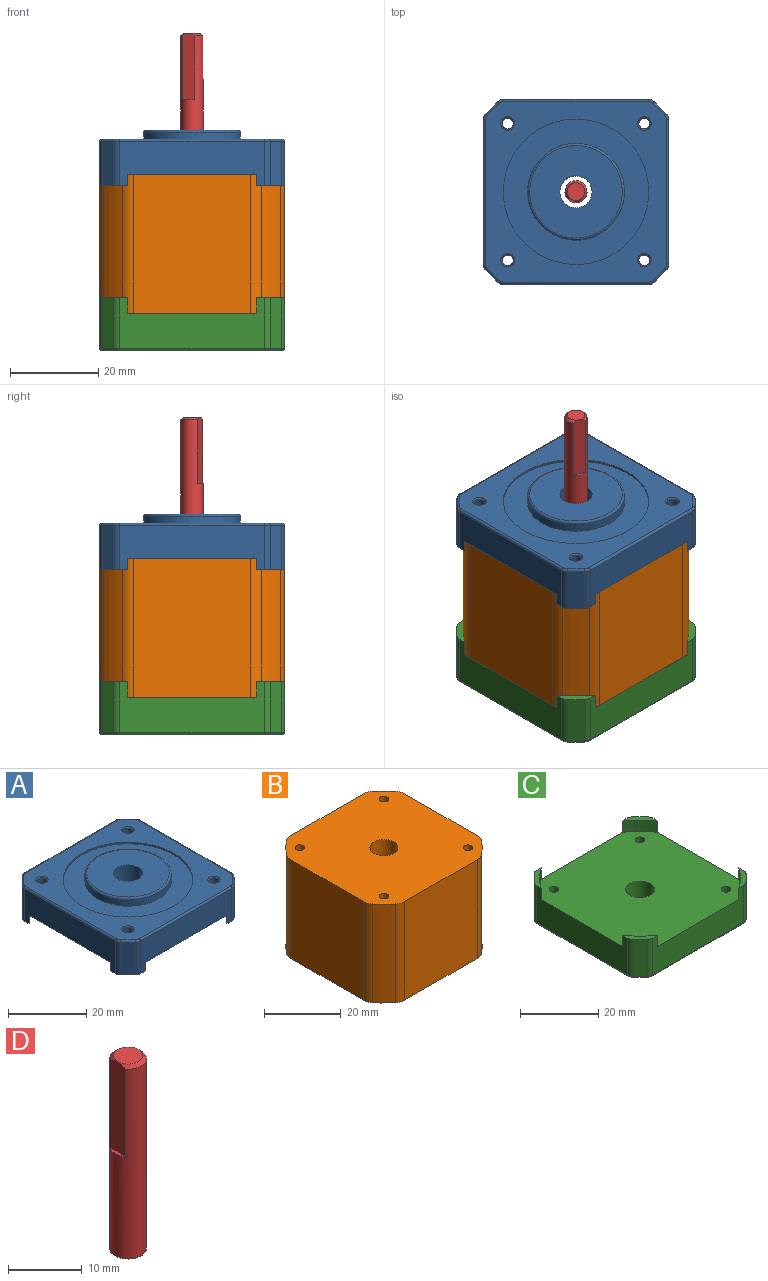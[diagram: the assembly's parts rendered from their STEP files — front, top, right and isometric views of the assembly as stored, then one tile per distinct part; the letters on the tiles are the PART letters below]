
ASSEMBLY  parts=4 mates=8
PART A: 56 faces, bbox 42.3x42.3x12.6 mm
  f0: plane 42x42mm, normal (0,0,-1), area 1631.2mm2, adj f2,f4,f6,f8,f9,f10,f11,f12
  f1: plane 10.1x2.63mm, normal (0.71,0.71,0), area 37.5mm2, adj f22,f27,f34,f39
  f2: plane 32.74x10.1mm, normal (0,1,0), area 254.6mm2, adj f0,f19,f20,f21,f22,f27,f28,f43
  f3: plane 10.1x2.63mm, normal (-0.71,0.71,0), area 37.5mm2, adj f20,f28,f29,f47
  f4: plane 32.74x10.1mm, normal (-1,0,0), area 254.6mm2, adj f0,f19,f20,f25,f26,f29,f30,f50
  f5: plane 10.1x2.63mm, normal (-0.71,-0.71,0), area 37.5mm2, adj f26,f30,f31,f46
  f6: plane 32.74x10.1mm, normal (0,-1,0), area 254.6mm2, adj f0,f23,f24,f25,f26,f31,f32,f42
  f7: plane 10.1x2.63mm, normal (0.71,-0.71,0), area 37.5mm2, adj f24,f32,f33,f38
  f8: cylinder r=1.25mm len=7.7mm, axis (0,0,-1), area 60.5mm2, adj f0,f54
  f9: cylinder r=1.25mm len=7.7mm, axis (0,0,-1), area 60.5mm2, adj f0,f55
  f10: cylinder r=1.25mm len=7.7mm, axis (0,0,-1), area 60.5mm2, adj f0,f52
  f11: cylinder r=3.65mm len=10mm, axis (0,0,-1), area 229.3mm2, adj f0,f16
  f12: cylinder r=1.25mm len=7.7mm, axis (0,0,-1), area 60.5mm2, adj f0,f53
  f13: plane 32.74x10.1mm, normal (1,0,0), area 254.6mm2, adj f0,f21,f22,f23,f24,f33,f34,f35
  f14: plane 41x41mm, normal (0,0,1), area 770.5mm2, adj f17,f35,f36,f37,f38,f39,f40,f41
  f15: cylinder r=11mm len=22mm, axis (0,0,-1), area 138.2mm2, adj f18,f51
  f16: plane 21x21mm, normal (0,0,1), area 304.5mm2, adj f11,f51
  f17: cylinder r=16.5mm len=33mm, axis (0,0,1), area 51.8mm2, adj f14,f18
  f18: plane 33x33mm, normal (0,0,1), area 475.2mm2, adj f15,f17
  f19: cylinder r=25.6mm len=6.36mm, axis (0,0,1), area 23.5mm2, adj f0,f2,f4,f20
  f20: plane 6.36x6.36mm, normal (0,0,-1), area 10.4mm2, adj f2,f3,f4,f19,f28,f29
  f21: cylinder r=25.6mm len=6.36mm, axis (0,0,1), area 23.5mm2, adj f0,f2,f13,f22
  f22: plane 6.36x6.36mm, normal (0,0,-1), area 10.4mm2, adj f1,f2,f13,f21,f27,f34
  f23: cylinder r=25.6mm len=6.36mm, axis (0,0,1), area 23.5mm2, adj f0,f6,f13,f24
  f24: plane 6.36x6.36mm, normal (0,0,-1), area 10.4mm2, adj f6,f7,f13,f23,f32,f33
  f25: cylinder r=25.6mm len=6.36mm, axis (0,0,1), area 23.5mm2, adj f0,f4,f6,f26
  f26: plane 6.36x6.36mm, normal (0,0,-1), area 10.4mm2, adj f4,f5,f6,f25,f30,f31
  f27: cylinder r=2mm len=10.1mm, axis (0,0,-1), area 15.9mm2, adj f1,f2,f22,f41
  f28: cylinder r=2mm len=10.1mm, axis (0,0,1), area 15.9mm2, adj f2,f3,f20,f45
  f29: cylinder r=2mm len=10.1mm, axis (0,0,-1), area 15.9mm2, adj f3,f4,f20,f49
  f30: cylinder r=2mm len=10.1mm, axis (0,0,1), area 15.9mm2, adj f4,f5,f26,f48
  f31: cylinder r=2mm len=10.1mm, axis (0,0,1), area 15.9mm2, adj f5,f6,f26,f44
  f32: cylinder r=2mm len=10.1mm, axis (0,0,-1), area 15.9mm2, adj f6,f7,f24,f40
  f33: cylinder r=2mm len=10.1mm, axis (0,0,1), area 15.9mm2, adj f7,f13,f24,f36
  f34: cylinder r=2mm len=10.1mm, axis (0,0,-1), area 15.9mm2, adj f1,f13,f22,f37
  f35: cylinder r=0.5mm len=32.74mm, axis (0,-1,0), area 25.7mm2, adj f13,f14,f36,f37
  f36: torus R=1.5mm, axis (0,0,1), area 1.1mm2, adj f14,f33,f35,f38
  f37: torus R=1.5mm, axis (0,0,1), area 1.1mm2, adj f14,f34,f35,f39
  f38: cylinder r=0.5mm len=2.98mm, axis (-0.71,-0.71,0), area 2.9mm2, adj f7,f14,f36,f40
  f39: cylinder r=0.5mm len=2.98mm, axis (0.71,-0.71,0), area 2.9mm2, adj f1,f14,f37,f41
  f40: torus R=1.5mm, axis (0,0,1), area 1.1mm2, adj f14,f32,f38,f42
  f41: torus R=1.5mm, axis (0,0,1), area 1.1mm2, adj f14,f27,f39,f43
  f42: cylinder r=0.5mm len=32.74mm, axis (-1,0,0), area 25.7mm2, adj f6,f14,f40,f44
  f43: cylinder r=0.5mm len=32.74mm, axis (1,0,0), area 25.7mm2, adj f2,f14,f41,f45
  f44: torus R=1.5mm, axis (0,0,1), area 1.1mm2, adj f14,f31,f42,f46
  f45: torus R=1.5mm, axis (0,0,1), area 1.1mm2, adj f14,f28,f43,f47
  f46: cylinder r=0.5mm len=2.98mm, axis (-0.71,0.71,0), area 2.9mm2, adj f5,f14,f44,f48
  f47: cylinder r=0.5mm len=2.98mm, axis (0.71,0.71,0), area 2.9mm2, adj f3,f14,f45,f49
  f48: torus R=1.5mm, axis (0,0,1), area 1.1mm2, adj f14,f30,f46,f50
  f49: torus R=1.5mm, axis (0,0,1), area 1.1mm2, adj f14,f29,f47,f50
  f50: cylinder r=0.5mm len=32.74mm, axis (0,1,0), area 25.7mm2, adj f4,f14,f48,f49
  f51: torus R=10.5mm, axis (0,0,1), area 53.4mm2, adj f15,f16
  f52: cone r=1.25mm half-angle=45deg, axis (0,0,1), area 3.7mm2, adj f10,f14
  f53: cone r=1.55mm half-angle=45deg, axis (0,0,1), area 3.7mm2, adj f12,f14
  f54: cone r=1.25mm half-angle=45deg, axis (0,0,1), area 3.7mm2, adj f8,f14
  f55: cone r=1.55mm half-angle=45deg, axis (0,0,1), area 3.7mm2, adj f9,f14
PART B: 23 faces, bbox 42x42x31.5 mm
  f0: cylinder r=25.6mm len=31.5mm, axis (0,0,1), area 194.5mm2, adj f13,f14,f15,f22
  f1: plane 31.5x26.65mm, normal (0,-1,0), area 839.5mm2, adj f13,f14,f15,f16
  f2: cylinder r=25.6mm len=31.5mm, axis (0,0,1), area 194.5mm2, adj f13,f14,f16,f17
  f3: plane 31.5x26.65mm, normal (-1,0,0), area 839.5mm2, adj f13,f14,f17,f18
  f4: cylinder r=25.6mm len=31.5mm, axis (0,0,1), area 194.5mm2, adj f13,f14,f18,f19
  f5: plane 31.5x26.65mm, normal (0,1,0), area 839.5mm2, adj f13,f14,f19,f20
  f6: cylinder r=25.6mm len=31.5mm, axis (0,0,1), area 194.5mm2, adj f13,f14,f20,f21
  f7: cylinder r=1.25mm len=31.5mm, axis (0,0,1), area 247.4mm2, adj f13,f14
  f8: plane 31.5x26.65mm, normal (1,0,0), area 839.5mm2, adj f13,f14,f21,f22
  f9: cylinder r=1.25mm len=31.5mm, axis (0,0,1), area 247.4mm2, adj f13,f14
  f10: cylinder r=1.25mm len=31.5mm, axis (0,0,1), area 247.4mm2, adj f13,f14
  f11: cylinder r=1.25mm len=31.5mm, axis (0,0,1), area 247.4mm2, adj f13,f14
  f12: cylinder r=3.65mm len=31.5mm, axis (0,0,1), area 722.4mm2, adj f13,f14
  f13: plane 42x42mm, normal (0,0,-1), area 1629.7mm2, adj f0,f1,f2,f3,f4,f5,f6,f7
  f14: plane 42x42mm, normal (0,0,1), area 1629.7mm2, adj f0,f1,f2,f3,f4,f5,f6,f7
  f15: cylinder r=4mm len=31.5mm, axis (0,0,1), area 83.8mm2, adj f0,f1,f13,f14
  f16: cylinder r=4mm len=31.5mm, axis (0,0,1), area 83.8mm2, adj f1,f2,f13,f14
  f17: cylinder r=4mm len=31.5mm, axis (0,0,1), area 83.8mm2, adj f2,f3,f13,f14
  f18: cylinder r=4mm len=31.5mm, axis (0,0,1), area 83.8mm2, adj f3,f4,f13,f14
  f19: cylinder r=4mm len=31.5mm, axis (0,0,1), area 83.8mm2, adj f4,f5,f13,f14
  f20: cylinder r=4mm len=31.5mm, axis (0,0,1), area 83.8mm2, adj f5,f6,f13,f14
  f21: cylinder r=4mm len=31.5mm, axis (0,0,1), area 83.8mm2, adj f6,f8,f13,f14
  f22: cylinder r=4mm len=31.5mm, axis (0,0,1), area 83.8mm2, adj f0,f8,f13,f14
PART C: 51 faces, bbox 42.3x42.3x12 mm
  f0: plane 42x42mm, normal (0,0,1), area 1631.2mm2, adj f1,f3,f5,f7,f8,f9,f10,f11
  f1: plane 32.74x11.5mm, normal (0,-1,0), area 274.1mm2, adj f0,f15,f16,f17,f18,f23,f26,f31
  f2: plane 11.5x2.63mm, normal (-0.71,-0.71,0), area 42.7mm2, adj f16,f23,f24,f35
  f3: plane 32.74x11.5mm, normal (-1,0,0), area 274.1mm2, adj f0,f15,f16,f21,f22,f24,f29,f39
  f4: plane 11.5x2.63mm, normal (-0.71,0.71,0), area 42.7mm2, adj f22,f29,f30,f43
  f5: plane 32.74x11.5mm, normal (0,1,0), area 274.1mm2, adj f0,f19,f20,f21,f22,f27,f30,f46
  f6: plane 11.5x2.63mm, normal (0.71,0.71,0), area 42.7mm2, adj f20,f27,f28,f42
  f7: plane 32.74x11.5mm, normal (1,0,0), area 274.1mm2, adj f0,f17,f18,f19,f20,f25,f28,f38
  f8: cylinder r=1.25mm len=6mm, axis (0,0,1), area 47.1mm2, adj f0,f48
  f9: cylinder r=3.65mm len=8.5mm, axis (0,0,1), area 194.9mm2, adj f0,f14
  f10: cylinder r=1.25mm len=6mm, axis (0,0,1), area 47.1mm2, adj f0,f47
  f11: cylinder r=1.25mm len=6mm, axis (0,0,1), area 47.1mm2, adj f0,f49
  f12: plane 11.5x2.63mm, normal (0.71,-0.71,0), area 42.7mm2, adj f18,f25,f26,f34
  f13: cylinder r=1.25mm len=6mm, axis (0,0,1), area 47.1mm2, adj f0,f50
  f14: plane 41x41mm, normal (0,0,-1), area 1437.4mm2, adj f9,f31,f32,f33,f34,f35,f36,f37
  f15: cylinder r=25.6mm len=6.36mm, axis (0,0,-1), area 31.6mm2, adj f0,f1,f3,f16
  f16: plane 6.36x6.36mm, normal (0,0,1), area 10.4mm2, adj f1,f2,f3,f15,f23,f24
  f17: cylinder r=25.6mm len=6.36mm, axis (0,0,-1), area 31.6mm2, adj f0,f1,f7,f18
  f18: plane 6.36x6.36mm, normal (0,0,1), area 10.4mm2, adj f1,f7,f12,f17,f25,f26
  f19: cylinder r=25.6mm len=6.36mm, axis (0,0,-1), area 31.6mm2, adj f0,f5,f7,f20
  f20: plane 6.36x6.36mm, normal (0,0,1), area 10.4mm2, adj f5,f6,f7,f19,f27,f28
  f21: cylinder r=25.6mm len=6.36mm, axis (0,0,-1), area 31.6mm2, adj f0,f3,f5,f22
  f22: plane 6.36x6.36mm, normal (0,0,1), area 10.4mm2, adj f3,f4,f5,f21,f29,f30
  f23: cylinder r=2mm len=11.5mm, axis (0,0,1), area 18.1mm2, adj f1,f2,f16,f33
  f24: cylinder r=2mm len=11.5mm, axis (0,0,1), area 18.1mm2, adj f2,f3,f16,f37
  f25: cylinder r=2mm len=11.5mm, axis (0,0,-1), area 18.1mm2, adj f7,f12,f18,f36
  f26: cylinder r=2mm len=11.5mm, axis (0,0,-1), area 18.1mm2, adj f1,f12,f18,f32
  f27: cylinder r=2mm len=11.5mm, axis (0,0,1), area 18.1mm2, adj f5,f6,f20,f44
  f28: cylinder r=2mm len=11.5mm, axis (0,0,1), area 18.1mm2, adj f6,f7,f20,f40
  f29: cylinder r=2mm len=11.5mm, axis (0,0,-1), area 18.1mm2, adj f3,f4,f22,f41
  f30: cylinder r=2mm len=11.5mm, axis (0,0,-1), area 18.1mm2, adj f4,f5,f22,f45
  f31: cylinder r=0.5mm len=32.74mm, axis (1,0,0), area 25.7mm2, adj f1,f14,f32,f33
  f32: torus R=1.5mm, axis (0,0,-1), area 1.1mm2, adj f14,f26,f31,f34
  f33: torus R=1.5mm, axis (0,0,-1), area 1.1mm2, adj f14,f23,f31,f35
  f34: cylinder r=0.5mm len=2.98mm, axis (0.71,0.71,0), area 2.9mm2, adj f12,f14,f32,f36
  f35: cylinder r=0.5mm len=2.98mm, axis (0.71,-0.71,0), area 2.9mm2, adj f2,f14,f33,f37
  f36: torus R=1.5mm, axis (0,0,-1), area 1.1mm2, adj f14,f25,f34,f38
  f37: torus R=1.5mm, axis (0,0,-1), area 1.1mm2, adj f14,f24,f35,f39
  f38: cylinder r=0.5mm len=32.74mm, axis (0,1,0), area 25.7mm2, adj f7,f14,f36,f40
  f39: cylinder r=0.5mm len=32.74mm, axis (0,-1,0), area 25.7mm2, adj f3,f14,f37,f41
  f40: torus R=1.5mm, axis (0,0,-1), area 1.1mm2, adj f14,f28,f38,f42
  f41: torus R=1.5mm, axis (0,0,-1), area 1.1mm2, adj f14,f29,f39,f43
  f42: cylinder r=0.5mm len=2.98mm, axis (-0.71,0.71,0), area 2.9mm2, adj f6,f14,f40,f44
  f43: cylinder r=0.5mm len=2.98mm, axis (-0.71,-0.71,0), area 2.9mm2, adj f4,f14,f41,f45
  f44: torus R=1.5mm, axis (0,0,-1), area 1.1mm2, adj f14,f27,f42,f46
  f45: torus R=1.5mm, axis (0,0,-1), area 1.1mm2, adj f14,f30,f43,f46
  f46: cylinder r=0.5mm len=32.74mm, axis (-1,0,0), area 25.7mm2, adj f5,f14,f44,f45
  f47: cone r=3.75mm half-angle=45deg, axis (0,0,-1), area 55.5mm2, adj f10,f14
  f48: cone r=1.25mm half-angle=45deg, axis (0,0,-1), area 55.5mm2, adj f8,f14
  f49: cone r=3.75mm half-angle=45deg, axis (0,0,-1), area 55.5mm2, adj f11,f14
  f50: cone r=1.25mm half-angle=45deg, axis (0,0,-1), area 55.5mm2, adj f13,f14
PART D: 6 faces, bbox 5x5x32 mm
  f0: plane 4x4mm, normal (0,0,1), area 12.6mm2, adj f5
  f1: cylinder r=2.5mm len=31.5mm, axis (0,0,-1), area 448.1mm2, adj f2,f3,f4,f5
  f2: plane 5x5mm, normal (0,0,-1), area 19.6mm2, adj f1
  f3: plane 15x3mm, normal (-1,0,0), area 44.5mm2, adj f1,f4,f5
  f4: plane 3x0.5mm, normal (0,0,1), area 1mm2, adj f1,f3
  f5: cone r=2mm half-angle=45deg, axis (0,0,-1), area 8.6mm2, adj f0,f1,f3
PLACE A t=(-13.22,11.58,-32.04)mm fixed
PLACE B t=(-13.22,11.58,-32.04)mm
PLACE C t=(-13.22,11.58,-32.04)mm
PLACE D rot(axis=(0,0,1),68deg) t=(-13.22,11.58,-32.04)mm
MATE cylindrical A.f10 <-> C.f11  axis (0,0,-1) through (2.28,-3.92,-24.34)mm
MATE cylindrical D.f1 <-> A.f11  axis (0,0,-1) through (-13.22,11.58,-16.29)mm
MATE cylindrical B.f9 <-> A.f9  axis (0,0,1) through (-28.72,-3.92,-32.04)mm
MATE planar D.f1 <-> A.f15  axis (0,0,1) through (-13.22,11.58,-0.04)mm
MATE cylindrical B.f10 <-> A.f10  axis (0,0,1) through (2.28,-3.92,-47.79)mm
MATE planar B.f12 <-> C.f19  axis (0,0,-1) through (-13.22,11.58,-63.54)mm
MATE planar B.f12 <-> A.f0  axis (0,0,1) through (-13.22,11.58,-32.04)mm
MATE cylindrical A.f9 <-> C.f8  axis (0,0,-1) through (-28.72,-3.92,-24.34)mm
